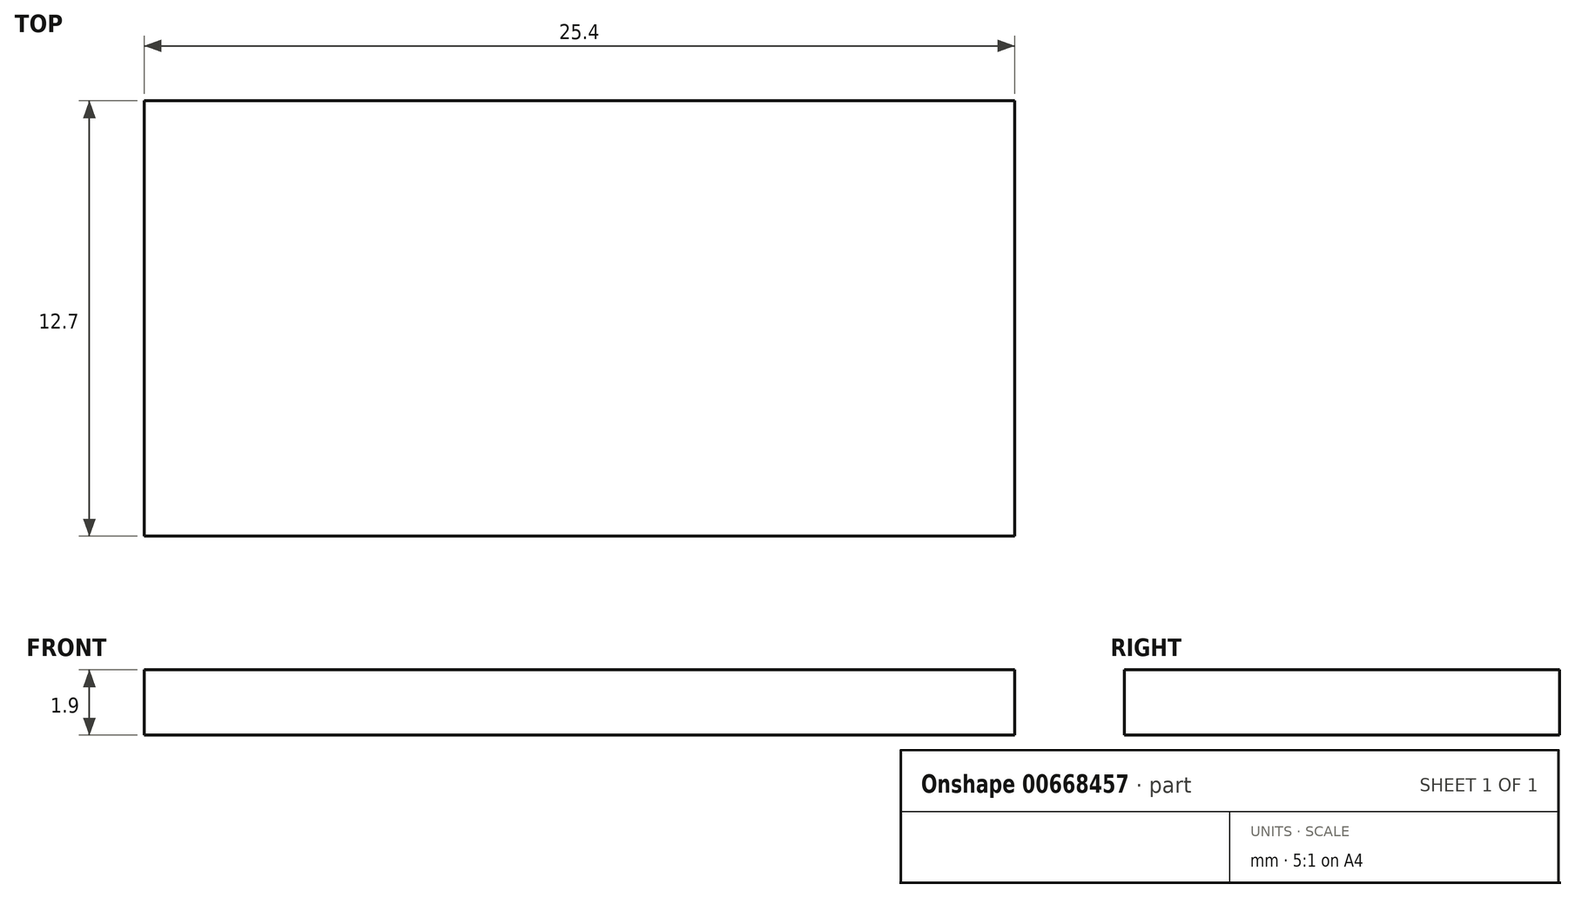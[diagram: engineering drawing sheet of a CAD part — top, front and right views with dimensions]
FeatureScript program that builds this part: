
annotation { "Feature Type Name" : "Feature", "Feature Type Description" : "" }
export const myFeature = defineFeature(function(context is Context, id is Id, definition is map)
    precondition{}
    {
        {
            var Q0;
            Q0=qCreatedBy(makeId("Top.planeOp"),FACE);
            var sketch = newSketch(context, id + "F0", { "sketchPlane" : qUnion([Q0])});
            skLineSegment(sketch, "E0.bottom", {"start": v(-16.62, 19.5) * mm, "end": v(8.78, 19.5) * mm});
            skLineSegment(sketch, "E0.top", {"start": v(-16.62, 6.8) * mm, "end": v(8.78, 6.8) * mm});
            skLineSegment(sketch, "E0.left", {"start": v(-16.62, 19.5) * mm, "end": v(-16.62, 6.8) * mm});
            skLineSegment(sketch, "E0.right", {"start": v(8.78, 19.5) * mm, "end": v(8.78, 6.8) * mm});
            skSolve(sketch);
        }
        {
            var Q0;
            Q0=makeQuery(id+"F0.imprint","IMPRINT",FACE,{"disambiguationData":[TD([[makeQuery(id+"F0.imprint","IMPRINT",EDGE,{"derivedFrom":sQuery(id+"F0.wireOp",EDGE,"E0.bottom")}),-1.0]])]});
            extrude(context, id + "F1", {"entities" : qUnion([Q0]), "depth" : 1.9 * mm});
        }
    });
